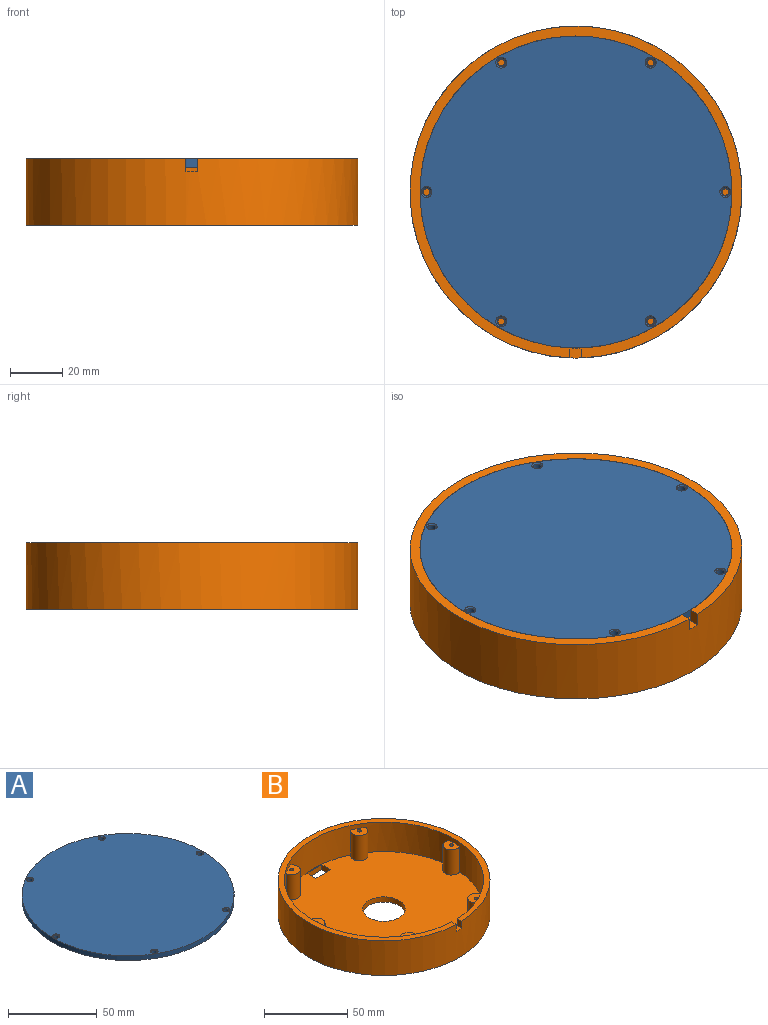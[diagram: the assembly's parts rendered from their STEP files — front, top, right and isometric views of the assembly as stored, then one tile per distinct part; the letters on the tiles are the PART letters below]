
ASSEMBLY  parts=2 mates=1
PART A: 15 faces, bbox 119.4x119.4x3.2 mm
  f0: cylinder r=1.65mm len=3.3mm, axis (0,0,-1), area 27.7mm2, adj f8,f13
  f1: cylinder r=1.65mm len=3.3mm, axis (0,0,-1), area 27.7mm2, adj f8,f14
  f2: cylinder r=1.65mm len=3.3mm, axis (0,0,-1), area 27.7mm2, adj f8,f9
  f3: cylinder r=1.65mm len=3.3mm, axis (0,0,-1), area 27.7mm2, adj f8,f10
  f4: cylinder r=1.65mm len=3.3mm, axis (0,0,-1), area 27.7mm2, adj f8,f11
  f5: cylinder r=1.65mm len=3.3mm, axis (0,0,-1), area 27.7mm2, adj f8,f12
  f6: cylinder r=59.69mm len=119.38mm, axis (0,0,-1), area 1190.8mm2, adj f7,f8
  f7: plane 119.38x119.38mm, normal (0,0,1), area 11110.6mm2, adj f6,f9,f10,f11,f12,f13,f14
  f8: plane 119.38x119.38mm, normal (0,0,-1), area 11141.8mm2, adj f0,f1,f2,f3,f4,f5,f6
  f9: cone r=1.65mm half-angle=41deg, axis (0,0,1), area 7.9mm2, adj f2,f7
  f10: cone r=1.65mm half-angle=41deg, axis (0,0,1), area 7.9mm2, adj f3,f7
  f11: cone r=1.65mm half-angle=41deg, axis (0,0,1), area 7.9mm2, adj f4,f7
  f12: cone r=1.65mm half-angle=41deg, axis (0,0,1), area 7.9mm2, adj f5,f7
  f13: cone r=1.65mm half-angle=41deg, axis (0,0,1), area 7.9mm2, adj f0,f7
  f14: cone r=1.65mm half-angle=41deg, axis (0,0,1), area 7.9mm2, adj f1,f7
PART B: 130 faces, bbox 127x127x25.4 mm
  f0: plane 127x127mm, normal (0,0,-1), area 11905.3mm2, adj f8,f29,f37,f38,f39,f40,f41,f42
  f1: plane 119.38x119.04mm, normal (0,0,1), area 10201.3mm2, adj f2,f3,f4,f5,f6,f7,f10,f29
  f2: cylinder r=5.08mm len=18.42mm, axis (0,0,1), area 384.7mm2, adj f1,f10,f16
  f3: cylinder r=5.08mm len=18.42mm, axis (0,0,1), area 384.7mm2, adj f1,f10,f15
  f4: cylinder r=5.08mm len=18.42mm, axis (0,0,1), area 384.7mm2, adj f1,f10,f14
  f5: cylinder r=5.08mm len=18.42mm, axis (0,0,1), area 384.7mm2, adj f1,f10,f13
  f6: cylinder r=5.08mm len=18.42mm, axis (0,0,1), area 384.7mm2, adj f1,f10,f12
  f7: cylinder r=5.08mm len=18.42mm, axis (0,0,1), area 384.7mm2, adj f1,f10,f11
  f8: cylinder r=63.5mm len=127mm, axis (0,0,-1), area 10111.4mm2, adj f0,f9,f123,f124,f125
  f9: plane 127x126.96mm, normal (0,0,1), area 1457.1mm2, adj f8,f10,f123,f125
  f10: cylinder r=59.69mm len=119.38mm, axis (0,0,-1), area 7080.7mm2, adj f1,f2,f3,f4,f5,f6,f7,f9
  f11: plane 10.16x7.62mm, normal (0,0,1), area 59.7mm2, adj f7,f10,f18
  f12: plane 10.16x9.38mm, normal (0,0,1), area 59.7mm2, adj f6,f10,f20
  f13: plane 10.16x9.38mm, normal (0,0,1), area 59.7mm2, adj f5,f10,f22
  f14: plane 10.16x7.62mm, normal (0,0,1), area 59.7mm2, adj f4,f10,f24
  f15: plane 10.16x9.38mm, normal (0,0,1), area 59.7mm2, adj f3,f10,f26
  f16: plane 10.16x9.38mm, normal (0,0,1), area 59.7mm2, adj f2,f10,f28
  f17: plane 2.54x2.54mm, normal (0,0,1), area 5.1mm2, adj f18
  f18: cylinder r=1.27mm len=14.61mm, axis (0,0,1), area 116.5mm2, adj f11,f17
  f19: plane 2.54x2.54mm, normal (0,0,1), area 5.1mm2, adj f20
  f20: cylinder r=1.27mm len=14.61mm, axis (0,0,1), area 116.5mm2, adj f12,f19
  f21: plane 2.54x2.54mm, normal (0,0,1), area 5.1mm2, adj f22
  f22: cylinder r=1.27mm len=14.61mm, axis (0,0,1), area 116.5mm2, adj f13,f21
  f23: plane 2.54x2.54mm, normal (0,0,1), area 5.1mm2, adj f24
  f24: cylinder r=1.27mm len=14.61mm, axis (0,0,1), area 116.5mm2, adj f14,f23
  f25: plane 2.54x2.54mm, normal (0,0,1), area 5.1mm2, adj f26
  f26: cylinder r=1.27mm len=14.61mm, axis (0,0,1), area 116.5mm2, adj f15,f25
  f27: plane 2.54x2.54mm, normal (0,0,1), area 5.1mm2, adj f28
  f28: cylinder r=1.27mm len=14.61mm, axis (0,0,1), area 116.5mm2, adj f16,f27
  f29: cylinder r=12.7mm len=25.4mm, axis (0,0,1), area 304mm2, adj f0,f1
  f30: extruded ~2.1x1.27mm, area 2.9mm2, adj f31,f56,f57,f122
  f31: extruded ~1.32x1.27mm, area 1.8mm2, adj f30,f32,f57,f122
  f32: extruded ~1.27x1.18mm, area 1.7mm2, adj f31,f33,f57,f122
  f33: extruded ~1.46x1.27mm, area 2.2mm2, adj f32,f34,f57,f122
  f34: extruded ~2.46x1.27mm, area 3.2mm2, adj f33,f35,f57,f122
  f35: plane 1.43x1.27mm, normal (-0.04,-1,0), area 1.8mm2, adj f34,f36,f57,f122
  f36: plane 1.27x0.85mm, normal (1,0,0), area 1.1mm2, adj f35,f56,f57,f122
  f37: plane 1.35x1.27mm, normal (0.98,-0.21,0), area 1.7mm2, adj f0,f38,f55,f57
  f38: plane 1.27x1.06mm, normal (0,-1,0), area 1.4mm2, adj f0,f37,f39,f57
  f39: plane 6.46x1.27mm, normal (-1,0,0), area 8.2mm2, adj f0,f38,f40,f57
  f40: extruded ~2.41x1.27mm, area 3.3mm2, adj f0,f39,f41,f57
  f41: extruded ~2.51x1.27mm, area 3.4mm2, adj f0,f40,f42,f57
  f42: extruded ~1.67x1.27mm, area 2.1mm2, adj f0,f41,f43,f57
  f43: extruded ~1.53x1.27mm, area 2.1mm2, adj f0,f42,f44,f57
  f44: plane 1.27x1.1mm, normal (0.93,-0.37,0), area 1.5mm2, adj f0,f43,f45,f57
  f45: extruded ~2.67x1.27mm, area 3.5mm2, adj f0,f44,f46,f57
  f46: extruded ~1.53x1.27mm, area 2.1mm2, adj f0,f45,f47,f57
  f47: extruded ~1.64x1.27mm, area 2.2mm2, adj f0,f46,f48,f57
  f48: plane 1.27x0.59mm, normal (1,0,0), area 0.7mm2, adj f0,f47,f49,f57
  f49: plane 1.61x1.27mm, normal (0.03,1,0), area 2mm2, adj f0,f48,f50,f57
  f50: extruded ~4.58x3mm, area 7.8mm2, adj f0,f49,f51,f57
  f51: extruded ~2.06x1.27mm, area 2.9mm2, adj f0,f50,f52,f57
  f52: extruded ~2.2x1.27mm, area 3mm2, adj f0,f51,f53,f57
  f53: extruded ~1.76x1.27mm, area 2.3mm2, adj f0,f52,f54,f57
  f54: extruded ~1.41x1.27mm, area 2.4mm2, adj f0,f53,f55,f57
  f55: plane 1.27x0.07mm, normal (0,-1,0), area 0.1mm2, adj f0,f37,f54,f57
  f56: extruded ~2.05x1.27mm, area 2.9mm2, adj f30,f36,f57,f122
  f57: plane 9.79x7.59mm, normal (0,0,-1), area 35.1mm2, adj f30,f31,f32,f33,f34,f35,f36,f37
  f58: plane 6.12x1.27mm, normal (1,0,0), area 7.8mm2, adj f0,f59,f75,f76
  f59: plane 1.43x1.27mm, normal (0,-1,0), area 1.8mm2, adj f0,f58,f60,f76
  f60: plane 6.17x1.27mm, normal (-1,0,0), area 7.8mm2, adj f0,f59,f61,f76
  f61: extruded ~2.62x1.27mm, area 3.6mm2, adj f0,f60,f62,f76
  f62: extruded ~2.6x1.27mm, area 3.6mm2, adj f0,f61,f63,f76
  f63: extruded ~1.78x1.27mm, area 2.3mm2, adj f0,f62,f64,f76
  f64: extruded ~1.27x1.2mm, area 2.1mm2, adj f0,f63,f65,f76
  f65: plane 1.27x0.09mm, normal (0,1,0), area 0.1mm2, adj f0,f64,f66,f76
  f66: extruded ~1.27x1.22mm, area 1.6mm2, adj f0,f65,f67,f76
  f67: plane 4.07x1.27mm, normal (-1,0,0), area 5.2mm2, adj f0,f66,f68,f76
  f68: plane 1.43x1.27mm, normal (0,1,0), area 1.8mm2, adj f0,f67,f69,f76
  f69: plane 13.43x1.27mm, normal (1,0,0), area 17.1mm2, adj f0,f68,f70,f76
  f70: plane 1.43x1.27mm, normal (0,-1,0), area 1.8mm2, adj f0,f69,f71,f76
  f71: plane 4.95x1.27mm, normal (-1,0,0), area 6.3mm2, adj f0,f70,f72,f76
  f72: extruded ~2.66x1.27mm, area 3.6mm2, adj f0,f71,f73,f76
  f73: extruded ~2.18x1.27mm, area 3.1mm2, adj f0,f72,f74,f76
  f74: extruded ~1.65x1.27mm, area 2.3mm2, adj f0,f73,f75,f76
  f75: extruded ~1.73x1.27mm, area 2.3mm2, adj f0,f58,f74,f76
  f76: plane 13.43x7.91mm, normal (0,0,-1), area 38.2mm2, adj f58,f59,f60,f61,f62,f63,f64,f65
  f77: extruded ~1.27x0.73mm, area 0.9mm2, adj f0,f78,f95,f96
  f78: extruded ~1.27x1.11mm, area 1.6mm2, adj f0,f77,f79,f96
  f79: extruded ~1.31x1.27mm, area 1.8mm2, adj f0,f78,f80,f96
  f80: plane 5.57x1.27mm, normal (-1,0,0), area 7.1mm2, adj f0,f79,f81,f96
  f81: plane 2.75x1.27mm, normal (0,-1,0), area 3.5mm2, adj f0,f80,f82,f96
  f82: plane 1.27x1.11mm, normal (-1,0,0), area 1.4mm2, adj f0,f81,f83,f96
  f83: plane 2.75x1.27mm, normal (0,1,0), area 3.5mm2, adj f0,f82,f84,f96
  f84: plane 2.19x1.27mm, normal (-1,0,0), area 2.8mm2, adj f0,f83,f85,f96
  f85: plane 1.27x0.83mm, normal (0,1,0), area 1.1mm2, adj f0,f84,f86,f96
  f86: plane 2.02x1.27mm, normal (0.96,0.29,0), area 2.7mm2, adj f0,f85,f87,f96
  f87: plane 1.36x1.27mm, normal (0.4,0.92,0), area 1.9mm2, adj f0,f86,f88,f96
  f88: plane 1.27x0.69mm, normal (1,0,0), area 0.9mm2, adj f0,f87,f89,f96
  f89: plane 1.36x1.27mm, normal (0,-1,0), area 1.7mm2, adj f0,f88,f90,f96
  f90: plane 5.63x1.27mm, normal (1,0,0), area 7.1mm2, adj f0,f89,f91,f96
  f91: extruded ~2.89x2.74mm, area 5.8mm2, adj f0,f90,f92,f96
  f92: extruded ~1.27x0.82mm, area 1mm2, adj f0,f91,f93,f96
  f93: extruded ~1.27x0.69mm, area 0.9mm2, adj f0,f92,f94,f96
  f94: plane 1.27x1.1mm, normal (-1,0,0), area 1.4mm2, adj f0,f93,f95,f96
  f95: extruded ~1.27x0.56mm, area 0.7mm2, adj f0,f77,f94,f96
  f96: plane 11.83x5.6mm, normal (0,0,-1), area 23.2mm2, adj f77,f78,f79,f80,f81,f82,f83,f84
  f97: extruded ~1.27x0.72mm, area 1mm2, adj f0,f98,f104,f105
  f98: extruded ~1.27x0.72mm, area 1mm2, adj f0,f97,f99,f105
  f99: extruded ~1.27x0.61mm, area 0.8mm2, adj f0,f98,f100,f105
  f100: extruded ~1.27x0.6mm, area 0.8mm2, adj f0,f99,f101,f105
  f101: extruded ~1.27x0.72mm, area 1mm2, adj f0,f100,f102,f105
  f102: extruded ~1.27x0.72mm, area 1mm2, adj f0,f101,f103,f105
  f103: extruded ~1.27x0.6mm, area 0.8mm2, adj f0,f102,f104,f105
  f104: extruded ~1.27x0.61mm, area 0.8mm2, adj f0,f97,f103,f105
  f105: plane 1.91x1.69mm, normal (0,0,-1), area 2.6mm2, adj f97,f98,f99,f100,f101,f102,f103,f104
  f106: plane 1.43x1.27mm, normal (0,-1,0), area 1.8mm2, adj f0,f107,f109,f110
  f107: plane 9.46x1.27mm, normal (-1,0,0), area 12mm2, adj f0,f106,f108,f110
  f108: plane 1.43x1.27mm, normal (0,1,0), area 1.8mm2, adj f0,f107,f109,f110
  f109: plane 9.46x1.27mm, normal (1,0,0), area 12mm2, adj f0,f106,f108,f110
  f110: plane 9.46x1.43mm, normal (0,0,-1), area 13.6mm2, adj f106,f107,f108,f109
  f111: plane 1.47x1.27mm, normal (0,-1,0), area 1.9mm2, adj f0,f112,f120,f121
  f112: plane 5.39x1.27mm, normal (-1,0,0), area 6.9mm2, adj f0,f111,f113,f121
  f113: plane 5.23x1.27mm, normal (0,-1,0), area 6.6mm2, adj f0,f112,f114,f121
  f114: plane 1.3x1.27mm, normal (-1,0,0), area 1.7mm2, adj f0,f113,f115,f121
  f115: plane 5.23x1.27mm, normal (0,1,0), area 6.6mm2, adj f0,f114,f116,f121
  f116: plane 4.62x1.27mm, normal (-1,0,0), area 5.9mm2, adj f0,f115,f117,f121
  f117: plane 5.57x1.27mm, normal (0,-1,0), area 7.1mm2, adj f0,f116,f118,f121
  f118: plane 1.3x1.27mm, normal (-1,0,0), area 1.7mm2, adj f0,f117,f119,f121
  f119: plane 7.04x1.27mm, normal (0,1,0), area 8.9mm2, adj f0,f118,f120,f121
  f120: plane 12.62x1.27mm, normal (1,0,0), area 16mm2, adj f0,f111,f119,f121
  f121: plane 12.62x7.04mm, normal (0,0,-1), area 32.6mm2, adj f111,f112,f113,f114,f115,f116,f117,f118
  f122: plane 4.65x3.64mm, normal (0,0,-1), area 13.7mm2, adj f30,f31,f32,f33,f34,f35,f36,f56
  f123: plane 4.98x3.81mm, normal (1,0,0), area 19mm2, adj f8,f9,f10,f124
  f124: plane 4.56x3.85mm, normal (0,0,1), area 17.4mm2, adj f8,f10,f123,f125
  f125: plane 4.98x3.81mm, normal (-1,0,0), area 19mm2, adj f8,f9,f10,f124
  f126: plane 7.62x3.81mm, normal (1,0,0), area 29mm2, adj f0,f1,f127,f129
  f127: plane 12.7x3.81mm, normal (0,-1,0), area 48.4mm2, adj f0,f1,f126,f128
  f128: plane 7.62x3.81mm, normal (-1,0,0), area 29mm2, adj f0,f1,f127,f129
  f129: plane 12.7x3.81mm, normal (0,1,0), area 48.4mm2, adj f0,f1,f126,f128
PLACE A t=(97.15,56.36,33.65)mm
PLACE B t=(97.15,56.36,11.43)mm
MATE fastened B.f4 <-> A.f2  axis (0,0,1) through (40,56.36,33.65)mm
